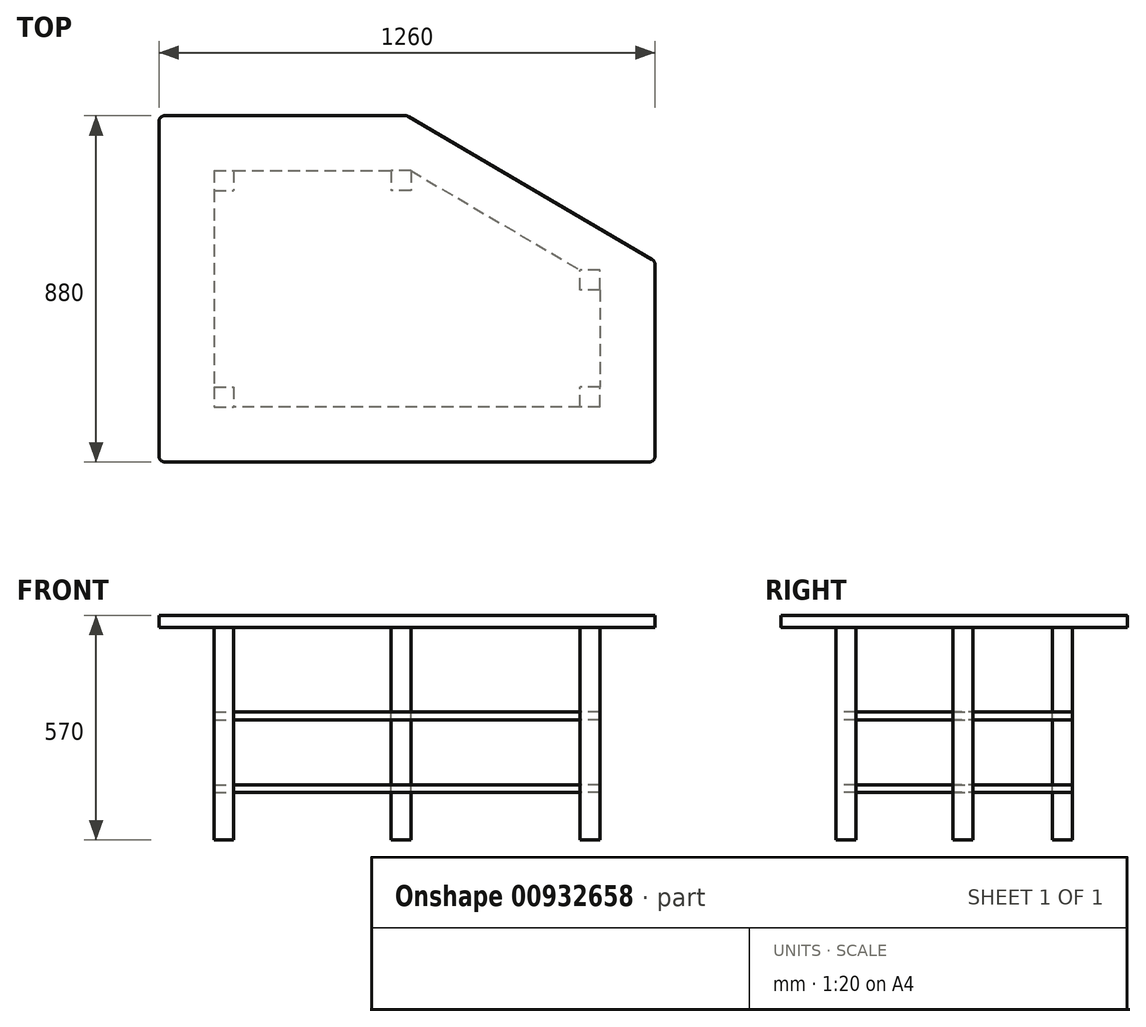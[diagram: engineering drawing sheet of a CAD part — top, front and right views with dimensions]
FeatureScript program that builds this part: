
annotation { "Feature Type Name" : "Feature", "Feature Type Description" : "" }
export const myFeature = defineFeature(function(context is Context, id is Id, definition is map)
    precondition{}
    {
        {
            var Q0;
            Q0=qCreatedBy(makeId("Top.planeOp"),FACE);
            var sketch = newSketch(context, id + "F0", { "sketchPlane" : qUnion([Q0])});
            skLineSegment(sketch, "E0", {"start": v(-85.72, 168.9) * mm, "end": v(525.2, 168.9) * mm});
            skLineSegment(sketch, "E1", {"start": v(532.8, 166.83) * mm, "end": v(1151.88, -196.76) * mm});
            skLineSegment(sketch, "E2", {"start": v(1159.28, -209.7) * mm, "end": v(1159.28, -696.1) * mm});
            skLineSegment(sketch, "E3", {"start": v(1144.28, -711.1) * mm, "end": v(-85.72, -711.1) * mm});
            skLineSegment(sketch, "E4", {"start": v(-100.72, -696.1) * mm, "end": v(-100.72, 153.9) * mm});
            skLineSegment(sketch, "E5.bottom", {"start": v(39.28, 28.9) * mm, "end": v(89.28, 28.9) * mm});
            skLineSegment(sketch, "E5.top", {"start": v(39.28, -21.1) * mm, "end": v(89.28, -21.1) * mm});
            skLineSegment(sketch, "E5.left", {"start": v(39.28, 28.9) * mm, "end": v(39.28, -21.1) * mm});
            skLineSegment(sketch, "E5.right", {"start": v(89.28, 28.9) * mm, "end": v(89.28, -21.1) * mm});
            skLineSegment(sketch, "E6.bottom", {"start": v(39.28, -521.1) * mm, "end": v(89.28, -521.1) * mm});
            skLineSegment(sketch, "E6.top", {"start": v(39.28, -571.1) * mm, "end": v(89.28, -571.1) * mm});
            skLineSegment(sketch, "E6.left", {"start": v(39.28, -521.1) * mm, "end": v(39.28, -571.1) * mm});
            skLineSegment(sketch, "E6.right", {"start": v(89.28, -521.1) * mm, "end": v(89.28, -571.1) * mm});
            skLineSegment(sketch, "E7.bottom", {"start": v(1019.28, -571.1) * mm, "end": v(969.28, -571.1) * mm});
            skLineSegment(sketch, "E7.top", {"start": v(1019.28, -521.1) * mm, "end": v(969.28, -521.1) * mm});
            skLineSegment(sketch, "E7.left", {"start": v(1019.28, -571.1) * mm, "end": v(1019.28, -521.1) * mm});
            skLineSegment(sketch, "E7.right", {"start": v(969.28, -571.1) * mm, "end": v(969.28, -521.1) * mm});
            skLineSegment(sketch, "E8.bottom", {"start": v(1019.28, -273.65) * mm, "end": v(969.28, -273.65) * mm});
            skLineSegment(sketch, "E8.top", {"start": v(1019.28, -223.65) * mm, "end": v(969.28, -223.65) * mm});
            skLineSegment(sketch, "E8.left", {"start": v(1019.28, -273.65) * mm, "end": v(1019.28, -223.65) * mm});
            skLineSegment(sketch, "E8.right", {"start": v(969.28, -273.65) * mm, "end": v(969.28, -223.65) * mm});
            skLineSegment(sketch, "E9.bottom", {"start": v(539.28, 28.9) * mm, "end": v(489.28, 28.9) * mm});
            skLineSegment(sketch, "E9.top", {"start": v(539.28, -21.1) * mm, "end": v(489.28, -21.1) * mm});
            skLineSegment(sketch, "E9.left", {"start": v(539.28, 28.9) * mm, "end": v(539.28, -21.1) * mm});
            skLineSegment(sketch, "E9.right", {"start": v(489.28, 28.9) * mm, "end": v(489.28, -21.1) * mm});
            skLineSegment(sketch, "E10", {"start": v(39.28, -21.1) * mm, "end": v(39.28, -521.1) * mm});
            skLineSegment(sketch, "E11", {"start": v(1019.28, -273.65) * mm, "end": v(1019.28, -521.1) * mm});
            skLineSegment(sketch, "E12", {"start": v(969.28, -571.1) * mm, "end": v(89.28, -571.1) * mm});
            skLineSegment(sketch, "E13", {"start": v(89.28, 28.9) * mm, "end": v(489.28, 28.9) * mm});
            skLineSegment(sketch, "E14", {"start": v(539.28, 28.9) * mm, "end": v(969.28, -223.65) * mm});
            skLineSegment(sketch, "E15", {"start": v(-100.72, 28.9) * mm, "end": v(39.28, 28.9) * mm, "construction": true});
            skLineSegment(sketch, "E16", {"start": v(1019.28, -397.38) * mm, "end": v(1159.28, -397.38) * mm, "construction": true});
            skLineSegment(sketch, "E17", {"start": v(39.28, 28.9) * mm, "end": v(39.28, 168.9) * mm, "construction": true});
            skLineSegment(sketch, "E18", {"start": v(39.28, -711.1) * mm, "end": v(39.28, -571.1) * mm, "construction": true});
            skPoint(sketch, "E19.visualSharp", {"position": v(-100.72, -711.1) * mm});
            skArc(sketch, "E19.filletArc", {"start": v(-100.72, -696.1) * mm, "mid": v(-96.32, -706.71) * mm, "end": v(-85.72, -711.1) * mm});
            skLineSegment(sketch, "E20", {"start": v(1019.28, -223.65) * mm, "end": v(1065.03, -145.75) * mm, "construction": true});
            skLineSegment(sketch, "E21", {"start": v(539.28, 28.9) * mm, "end": v(597.85, 128.62) * mm, "construction": true});
            skPoint(sketch, "E22.visualSharp", {"position": v(1159.28, -711.1) * mm});
            skArc(sketch, "E22.filletArc", {"start": v(1144.28, -711.1) * mm, "mid": v(1154.89, -706.71) * mm, "end": v(1159.28, -696.1) * mm});
            skPoint(sketch, "E23.visualSharp", {"position": v(-100.72, 168.9) * mm});
            skArc(sketch, "E23.filletArc", {"start": v(-85.72, 168.9) * mm, "mid": v(-96.32, 164.5) * mm, "end": v(-100.72, 153.9) * mm});
            skPoint(sketch, "E24.visualSharp", {"position": v(1159.28, -201.1) * mm});
            skArc(sketch, "E24.filletArc", {"start": v(1159.28, -209.7) * mm, "mid": v(1157.3, -202.24) * mm, "end": v(1151.88, -196.76) * mm});
            skPoint(sketch, "E25.visualSharp", {"position": v(529.28, 168.9) * mm});
            skArc(sketch, "E25.filletArc", {"start": v(532.8, 166.83) * mm, "mid": v(529.14, 168.37) * mm, "end": v(525.2, 168.9) * mm});
            skSolve(sketch);
        }
        {
            var Q0;
            Q0=qCreatedBy(makeId("Front.planeOp"),FACE);
            var sketch = newSketch(context, id + "F1", { "sketchPlane" : qUnion([Q0])});
            skLineSegment(sketch, "E26.bottom", {"start": v(39.28, -4.46) * mm, "end": v(89.28, -4.46) * mm});
            skLineSegment(sketch, "E26.top", {"start": v(39.28, -544.46) * mm, "end": v(89.28, -544.46) * mm});
            skLineSegment(sketch, "E26.left", {"start": v(39.28, -4.46) * mm, "end": v(39.28, -544.46) * mm});
            skLineSegment(sketch, "E26.right", {"start": v(89.28, -4.46) * mm, "end": v(89.28, -544.46) * mm});
            skLineSegment(sketch, "E27.bottom", {"start": v(1019.28, -4.46) * mm, "end": v(969.28, -4.46) * mm});
            skLineSegment(sketch, "E27.top", {"start": v(1019.28, -544.46) * mm, "end": v(969.28, -544.46) * mm});
            skLineSegment(sketch, "E27.left", {"start": v(1019.28, -4.46) * mm, "end": v(1019.28, -544.46) * mm});
            skLineSegment(sketch, "E27.right", {"start": v(969.28, -4.46) * mm, "end": v(969.28, -544.46) * mm});
            skLineSegment(sketch, "E28.bottom", {"start": v(539.28, -4.46) * mm, "end": v(489.28, -4.46) * mm});
            skLineSegment(sketch, "E28.top", {"start": v(539.28, -544.46) * mm, "end": v(489.28, -544.46) * mm});
            skLineSegment(sketch, "E28.left", {"start": v(539.28, -4.46) * mm, "end": v(539.28, -544.46) * mm});
            skLineSegment(sketch, "E28.right", {"start": v(489.28, -4.46) * mm, "end": v(489.28, -544.46) * mm});
            skLineSegment(sketch, "E29", {"start": v(89.28, -4.46) * mm, "end": v(489.28, -4.46) * mm});
            skLineSegment(sketch, "E30", {"start": v(539.28, -4.46) * mm, "end": v(969.28, -4.46) * mm});
            skLineSegment(sketch, "E31", {"start": v(39.28, -4.46) * mm, "end": v(-100.72, -4.46) * mm});
            skLineSegment(sketch, "E32", {"start": v(-100.72, -4.46) * mm, "end": v(-100.72, 25.54) * mm});
            skLineSegment(sketch, "E33", {"start": v(-100.72, 25.54) * mm, "end": v(1159.28, 25.54) * mm});
            skLineSegment(sketch, "E34", {"start": v(1159.28, 25.54) * mm, "end": v(1159.28, -4.46) * mm});
            skLineSegment(sketch, "E35", {"start": v(1159.28, -4.46) * mm, "end": v(1019.28, -4.46) * mm});
            skLineSegment(sketch, "E36.bottom", {"start": v(89.28, -424.46) * mm, "end": v(489.28, -424.46) * mm});
            skLineSegment(sketch, "E36.top", {"start": v(89.28, -219.46) * mm, "end": v(489.28, -219.46) * mm});
            skLineSegment(sketch, "E36.left", {"start": v(89.28, -424.46) * mm, "end": v(89.28, -219.46) * mm});
            skLineSegment(sketch, "E36.right", {"start": v(489.28, -424.46) * mm, "end": v(489.28, -219.46) * mm});
            skLineSegment(sketch, "E37.bottom", {"start": v(539.28, -424.46) * mm, "end": v(969.28, -424.46) * mm});
            skLineSegment(sketch, "E37.top", {"start": v(539.28, -219.46) * mm, "end": v(969.28, -219.46) * mm});
            skLineSegment(sketch, "E37.left", {"start": v(539.28, -424.46) * mm, "end": v(539.28, -219.46) * mm});
            skLineSegment(sketch, "E37.right", {"start": v(969.28, -424.46) * mm, "end": v(969.28, -219.46) * mm});
            skLineSegment(sketch, "E38", {"start": v(489.28, -424.46) * mm, "end": v(539.28, -424.46) * mm});
            skLineSegment(sketch, "E39", {"start": v(489.28, -219.46) * mm, "end": v(539.28, -219.46) * mm});
            skLineSegment(sketch, "E40", {"start": v(89.28, -239.46) * mm, "end": v(489.28, -239.46) * mm});
            skLineSegment(sketch, "E41", {"start": v(489.28, -239.46) * mm, "end": v(539.28, -239.46) * mm});
            skLineSegment(sketch, "E42", {"start": v(539.28, -239.46) * mm, "end": v(969.28, -239.46) * mm});
            skLineSegment(sketch, "E43", {"start": v(89.28, -404.46) * mm, "end": v(489.28, -404.46) * mm});
            skLineSegment(sketch, "E44", {"start": v(122.23, -424.46) * mm, "end": v(122.23, -404.46) * mm, "construction": true});
            skLineSegment(sketch, "E45", {"start": v(122.16, -239.46) * mm, "end": v(122.16, -219.46) * mm, "construction": true});
            skLineSegment(sketch, "E46", {"start": v(489.28, -404.46) * mm, "end": v(539.28, -404.46) * mm});
            skLineSegment(sketch, "E47", {"start": v(539.28, -404.46) * mm, "end": v(969.28, -404.46) * mm});
            skSolve(sketch);
        }
        {
            var Q0;
            Q0=makeQuery(id+"F0.imprint","IMPRINT",FACE,{"disambiguationData":[TD([[makeQuery(id+"F0.imprint","IMPRINT",EDGE,{"derivedFrom":sQuery(id+"F0.wireOp",EDGE,"E6.bottom")}),-1.0]])]});
            var Q1;
            Q1=makeQuery(id+"F0.imprint","IMPRINT",FACE,{"disambiguationData":[TD([[makeQuery(id+"F0.imprint","IMPRINT",EDGE,{"derivedFrom":sQuery(id+"F0.wireOp",EDGE,"E7.bottom")}),-1.0]])]});
            var Q2;
            Q2=makeQuery(id+"F0.imprint","IMPRINT",FACE,{"disambiguationData":[TD([[makeQuery(id+"F0.imprint","IMPRINT",EDGE,{"derivedFrom":sQuery(id+"F0.wireOp",EDGE,"E8.bottom")}),-1.0]])]});
            var Q3;
            Q3=makeQuery(id+"F0.imprint","IMPRINT",FACE,{"disambiguationData":[TD([[makeQuery(id+"F0.imprint","IMPRINT",EDGE,{"derivedFrom":sQuery(id+"F0.wireOp",EDGE,"E9.bottom")}),1.0]])]});
            var Q4;
            Q4=makeQuery(id+"F0.imprint","IMPRINT",FACE,{"disambiguationData":[TD([[makeQuery(id+"F0.imprint","IMPRINT",EDGE,{"derivedFrom":sQuery(id+"F0.wireOp",EDGE,"E5.bottom")}),-1.0]])]});
            var Q5;
            Q5=sQuery(id+"F1.wireOp",VERTEX,"E26.top.start");
            var Q6;
            Q6=sQuery(id+"F1.wireOp",VERTEX,"E26.bottom.start");
            extrude(context, id + "F2", {"entities" : qUnion([Q0, Q1, Q2, Q3, Q4]), "endBound" : BoundingType.UP_TO_VERTEX, "oppositeDirection" : true, "depth" : 25 * mm, "endBoundEntityVertex" : qUnion([Q5]), "offsetDistance" : 25 * mm, "hasSecondDirection" : true, "secondDirectionBound" : SecondDirectionBoundingType.UP_TO_VERTEX, "secondDirectionOppositeDirection" : true, "secondDirectionDepth" : 25 * mm, "secondDirectionBoundEntityVertex" : qUnion([Q6])});
        }
        {
            var Q0;
            Q0=makeQuery(id+"F0.imprint","IMPRINT",FACE,{"disambiguationData":[TD([[makeQuery(id+"F0.imprint","IMPRINT",EDGE,{"derivedFrom":sQuery(id+"F0.wireOp",EDGE,"E6.bottom")}),-1.0]])]});
            var Q1;
            Q1=makeQuery(id+"F0.imprint","IMPRINT",FACE,{"disambiguationData":[TD([[makeQuery(id+"F0.imprint","IMPRINT",EDGE,{"derivedFrom":sQuery(id+"F0.wireOp",EDGE,"E7.bottom")}),-1.0]])]});
            var Q2;
            Q2=makeQuery(id+"F0.imprint","IMPRINT",FACE,{"disambiguationData":[TD([[makeQuery(id+"F0.imprint","IMPRINT",EDGE,{"derivedFrom":sQuery(id+"F0.wireOp",EDGE,"E8.bottom")}),-1.0]])]});
            var Q3;
            Q3=makeQuery(id+"F0.imprint","IMPRINT",FACE,{"disambiguationData":[TD([[makeQuery(id+"F0.imprint","IMPRINT",EDGE,{"derivedFrom":sQuery(id+"F0.wireOp",EDGE,"E9.bottom")}),1.0]])]});
            var Q4;
            Q4=makeQuery(id+"F0.imprint","IMPRINT",FACE,{"disambiguationData":[TD([[makeQuery(id+"F0.imprint","IMPRINT",EDGE,{"derivedFrom":sQuery(id+"F0.wireOp",EDGE,"E5.bottom")}),-1.0]])]});
            var Q5;
            {var subQ1=sQuery(id+"F0.wireOp",EDGE,"E5.top");Q5=makeQuery(id+"F0.imprint","IMPRINT",FACE,{"disambiguationData":[TD([[makeQuery(id+"F0.imprint","IMPRINT",EDGE,{"derivedFrom":subQ1}),-1.0]])]});}
            var Q6;
            Q6=makeQuery(id+"F0.imprint","IMPRINT",FACE,{"disambiguationData":[TD([[makeQuery(id+"F0.imprint","IMPRINT",EDGE,{"derivedFrom":sQuery(id+"F0.wireOp",EDGE,"E0")}),-1.0]])]});
            var Q7;
            {var subQ1=sQuery(id+"F0.wireOp",EDGE,"E6.bottom");Q7=makeQuery(id+"F0.imprint","IMPRINT",FACE,{"disambiguationData":[TD([[makeQuery(id+"F0.imprint","IMPRINT",EDGE,{"derivedFrom":subQ1}),1.0]])]});}
            var Q8;
            {var subQ2=sQuery(id+"F0.wireOp",EDGE,"E8.bottom");Q8=makeQuery(id+"F0.imprint","IMPRINT",FACE,{"disambiguationData":[TD([[makeQuery(id+"F0.imprint","IMPRINT",EDGE,{"derivedFrom":subQ2}),1.0]])]});}
            var Q9;
            Q9=sQuery(id+"F1.wireOp",VERTEX,"E31.end");
            var Q10;
            Q10=sQuery(id+"F1.wireOp",VERTEX,"E32.end");
            extrude(context, id + "F3", {"entities" : qUnion([Q0, Q1, Q2, Q3, Q4, Q5, Q6, Q7, Q8]), "endBound" : BoundingType.UP_TO_VERTEX, "oppositeDirection" : true, "depth" : 25 * mm, "endBoundEntityVertex" : qUnion([Q9]), "offsetDistance" : 25 * mm, "hasSecondDirection" : true, "secondDirectionBound" : SecondDirectionBoundingType.UP_TO_VERTEX, "secondDirectionOppositeDirection" : false, "secondDirectionDepth" : 25 * mm, "secondDirectionBoundEntityVertex" : qUnion([Q10])});
        }
        {
            var Q0;
            {var subQ1=sQuery(id+"F0.wireOp",EDGE,"E5.top");Q0=makeQuery(id+"F0.imprint","IMPRINT",FACE,{"disambiguationData":[TD([[makeQuery(id+"F0.imprint","IMPRINT",EDGE,{"derivedFrom":subQ1}),-1.0]])]});}
            var Q1;
            {var subQ1=sQuery(id+"F0.wireOp",EDGE,"E6.bottom");Q1=makeQuery(id+"F0.imprint","IMPRINT",FACE,{"disambiguationData":[TD([[makeQuery(id+"F0.imprint","IMPRINT",EDGE,{"derivedFrom":subQ1}),1.0]])]});}
            var Q2;
            {var subQ2=sQuery(id+"F0.wireOp",EDGE,"E8.bottom");Q2=makeQuery(id+"F0.imprint","IMPRINT",FACE,{"disambiguationData":[TD([[makeQuery(id+"F0.imprint","IMPRINT",EDGE,{"derivedFrom":subQ2}),1.0]])]});}
            var Q3;
            Q3=sQuery(id+"F1.wireOp",VERTEX,"E44.start");
            var Q4;
            Q4=sQuery(id+"F1.wireOp",VERTEX,"E44.end");
            extrude(context, id + "F4", {"entities" : qUnion([Q0, Q1, Q2]), "endBound" : BoundingType.UP_TO_VERTEX, "oppositeDirection" : true, "depth" : 25 * mm, "endBoundEntityVertex" : qUnion([Q3]), "offsetDistance" : 25 * mm, "hasSecondDirection" : true, "secondDirectionBound" : SecondDirectionBoundingType.UP_TO_VERTEX, "secondDirectionOppositeDirection" : true, "secondDirectionDepth" : 25 * mm, "secondDirectionBoundEntityVertex" : qUnion([Q4])});
        }
        {
            var Q0;
            {var subQ1=sQuery(id+"F0.wireOp",EDGE,"E6.bottom");Q0=makeQuery(id+"F0.imprint","IMPRINT",FACE,{"disambiguationData":[TD([[makeQuery(id+"F0.imprint","IMPRINT",EDGE,{"derivedFrom":subQ1}),1.0]])]});}
            var Q1;
            {var subQ2=sQuery(id+"F0.wireOp",EDGE,"E8.bottom");Q1=makeQuery(id+"F0.imprint","IMPRINT",FACE,{"disambiguationData":[TD([[makeQuery(id+"F0.imprint","IMPRINT",EDGE,{"derivedFrom":subQ2}),1.0]])]});}
            var Q2;
            {var subQ1=sQuery(id+"F0.wireOp",EDGE,"E5.top");Q2=makeQuery(id+"F0.imprint","IMPRINT",FACE,{"disambiguationData":[TD([[makeQuery(id+"F0.imprint","IMPRINT",EDGE,{"derivedFrom":subQ1}),-1.0]])]});}
            var Q3;
            Q3=sQuery(id+"F1.wireOp",VERTEX,"E45.start");
            var Q4;
            Q4=sQuery(id+"F1.wireOp",VERTEX,"E45.end");
            extrude(context, id + "F5", {"entities" : qUnion([Q0, Q1, Q2]), "endBound" : BoundingType.UP_TO_VERTEX, "oppositeDirection" : true, "depth" : 25 * mm, "endBoundEntityVertex" : qUnion([Q3]), "offsetDistance" : 25 * mm, "hasSecondDirection" : true, "secondDirectionBound" : SecondDirectionBoundingType.UP_TO_VERTEX, "secondDirectionOppositeDirection" : true, "secondDirectionDepth" : 25 * mm, "secondDirectionBoundEntityVertex" : qUnion([Q4])});
        }
    });
